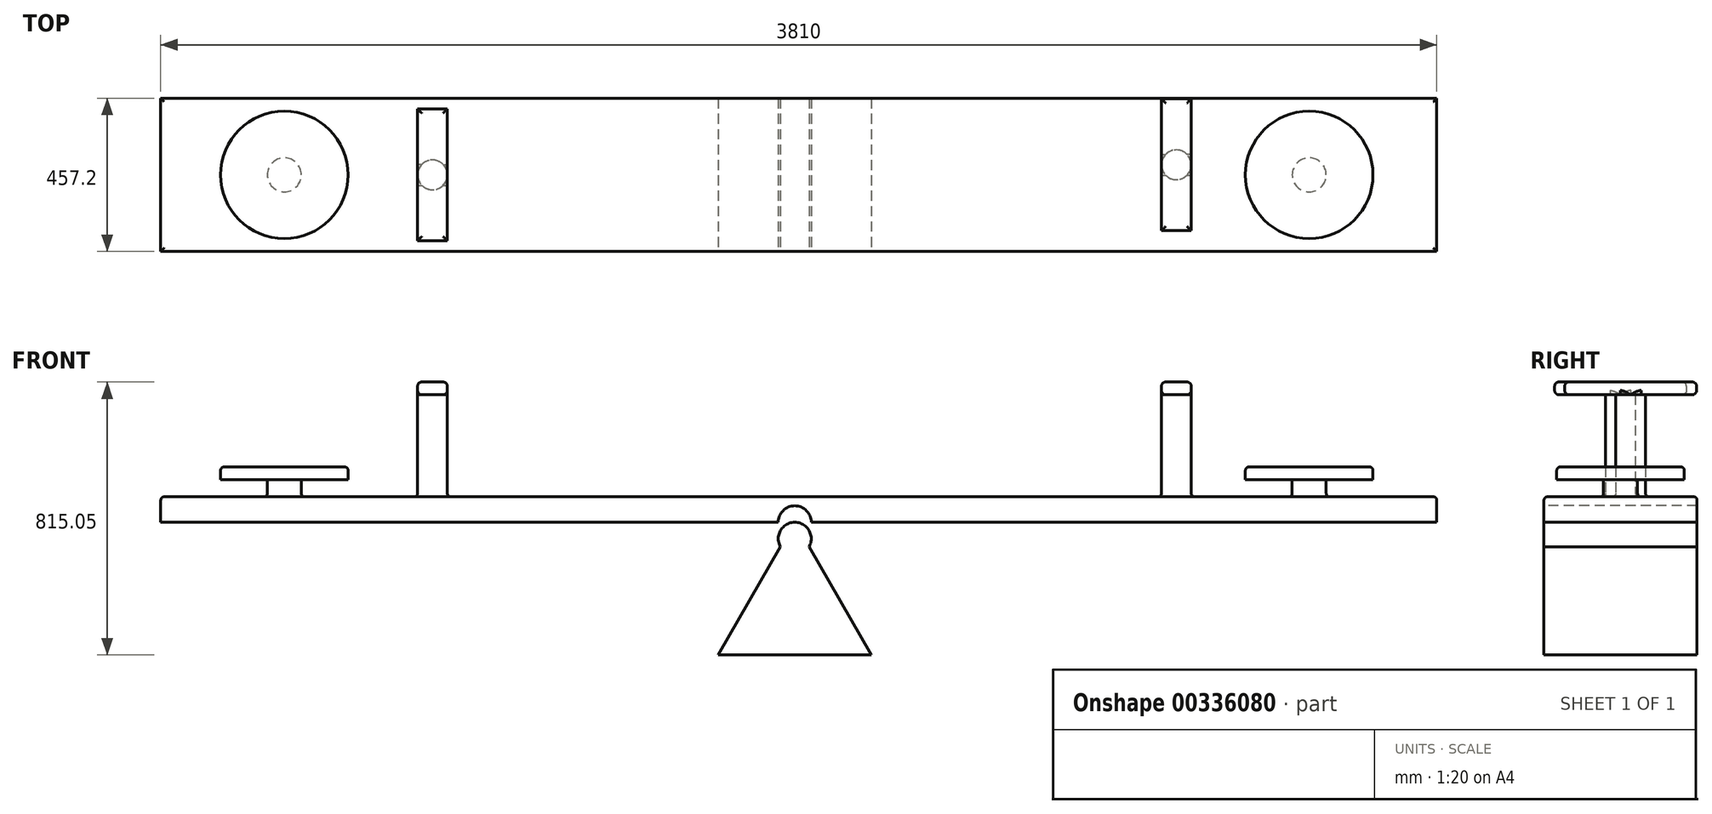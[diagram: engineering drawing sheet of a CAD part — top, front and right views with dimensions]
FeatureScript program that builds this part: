
annotation { "Feature Type Name" : "Feature", "Feature Type Description" : "" }
export const myFeature = defineFeature(function(context is Context, id is Id, definition is map)
    precondition{}
    {
        {
            var Q0;
            Q0=qCreatedBy(makeId("Top.planeOp"),FACE);
            var sketch = newSketch(context, id + "F0", { "sketchPlane" : qUnion([Q0])});
            skLineSegment(sketch, "E0.bottom", {"start": v(228.6, 228.6) * mm, "end": v(-228.6, 228.6) * mm});
            skLineSegment(sketch, "E0.top", {"start": v(228.6, -228.6) * mm, "end": v(-228.6, -228.6) * mm});
            skLineSegment(sketch, "E0.left", {"start": v(228.6, 228.6) * mm, "end": v(228.6, -228.6) * mm});
            skLineSegment(sketch, "E0.right", {"start": v(-228.6, 228.6) * mm, "end": v(-228.6, -228.6) * mm});
            skPoint(sketch, "E0.middle", {"position": v(0, 0) * mm});
            skSolve(sketch);
        }
        {
            var Q0;
            Q0=qCreatedBy(makeId("Front.planeOp"),FACE);
            cPlane(context, id + "F1", {"entities" : qUnion([Q0]), "cplaneType" : CPlaneType.OFFSET, "offset" : 228.6 * mm, "width" : 152.4 * mm, "height" : 152.4 * mm});
        }
        {
            var Q0;
            Q0=qCreatedBy(id+"F1.planeOp",FACE);
            var sketch = newSketch(context, id + "F2", { "sketchPlane" : qUnion([Q0])});
            skLineSegment(sketch, "E1", {"start": v(-228.6, 0) * mm, "end": v(-42.62, 322.13) * mm});
            skLineSegment(sketch, "E2", {"start": v(42.62, 322.13) * mm, "end": v(228.6, 0) * mm});
            skArc(sketch, "E3", {"start": v(42.62, 322.13) * mm, "mid": v(0, 395.95) * mm, "end": v(-42.62, 322.13) * mm});
            skPoint(sketch, "E4.orphan", {"position": v(0, 395.95) * mm});
            skLineSegment(sketch, "E5", {"start": v(-228.6, 0) * mm, "end": v(228.6, 0) * mm});
            skSolve(sketch);
        }
        {
            var Q0;
            Q0=makeQuery(id+"F0.imprint","IMPRINT",FACE,{"disambiguationData":[TD([[makeQuery(id+"F0.imprint","IMPRINT",EDGE,{"derivedFrom":sQuery(id+"F0.wireOp",EDGE,"E0.bottom")}),1.0]])]});
            cPlane(context, id + "F3", {"entities" : qUnion([Q0]), "cplaneType" : CPlaneType.OFFSET, "offset" : 395.95 * mm, "width" : 152.4 * mm, "height" : 152.4 * mm});
        }
        {
            var Q0;
            Q0=qCreatedBy(id+"F3.planeOp",FACE);
            var sketch = newSketch(context, id + "F4", { "sketchPlane" : qUnion([Q0])});
            skLineSegment(sketch, "E6.bottom", {"start": v(1917, 228.6) * mm, "end": v(-1893, 228.6) * mm});
            skLineSegment(sketch, "E6.top", {"start": v(1917, -228.6) * mm, "end": v(-1893, -228.6) * mm});
            skLineSegment(sketch, "E6.left", {"start": v(1917, 228.6) * mm, "end": v(1917, -228.6) * mm});
            skLineSegment(sketch, "E6.right", {"start": v(-1893, 228.6) * mm, "end": v(-1893, -228.6) * mm});
            skPoint(sketch, "E6.middle", {"position": v(12, 0) * mm});
            skSolve(sketch);
        }
        {
            var Q0;
            Q0 = qSketchRegion(id + "F4", true);
            extrude(context, id + "F5", {"entities" : qUnion([Q0]), "depth" : 76.2 * mm});
        }
        {
            var Q0;
            Q0=makeQuery(id+"F5.opExtrude","CAP_FACE",FACE,{"disambiguationData":[OSD([sQuery(id+"F4.wireOp",EDGE,"E6.bottom"),sQuery(id+"F4.wireOp",EDGE,"E6.top"),sQuery(id+"F4.wireOp",EDGE,"E6.left"),sQuery(id+"F4.wireOp",EDGE,"E6.right")])],"isStart":false});
            var sketch = newSketch(context, id + "F6", { "sketchPlane" : qUnion([Q0])});
            skCircle(sketch, "E7", {"center": v(-1524, 0) * mm, "radius": 50.8 * mm});
            skSolve(sketch);
        }
        {
            var Q0;
            Q0 = qSketchRegion(id + "F6", true);
            extrude(context, id + "F7", {"entities" : qUnion([Q0]), "operationType" : NewBodyOperationType.ADD, "depth" : 50.8 * mm});
        }
        {
            var Q0;
            Q0=makeQuery(id+"F7.opExtrude","CAP_FACE",FACE,{"disambiguationData":[OSD([sQuery(id+"F6.wireOp",EDGE,"E7")])],"isStart":false});
            var sketch = newSketch(context, id + "F8", { "sketchPlane" : qUnion([Q0])});
            skCircle(sketch, "E8", {"center": v(-1524, 0) * mm, "radius": 190.5 * mm});
            skSolve(sketch);
        }
        {
            var Q0;
            Q0 = qSketchRegion(id + "F8", true);
            extrude(context, id + "F9", {"entities" : qUnion([Q0]), "operationType" : NewBodyOperationType.ADD, "depth" : 38.1 * mm});
        }
        {
            var Q0;
            Q0=makeQuery(id+"F5.opExtrude","CAP_FACE",FACE,{"disambiguationData":[OSD([sQuery(id+"F4.wireOp",EDGE,"E6.bottom"),sQuery(id+"F4.wireOp",EDGE,"E6.top"),sQuery(id+"F4.wireOp",EDGE,"E6.left"),sQuery(id+"F4.wireOp",EDGE,"E6.right")])],"isStart":false});
            var sketch = newSketch(context, id + "F10", { "sketchPlane" : qUnion([Q0])});
            skCircle(sketch, "E9", {"center": v(1536, 0) * mm, "radius": 50.8 * mm});
            skSolve(sketch);
        }
        {
            var Q0;
            Q0 = qSketchRegion(id + "F10", true);
            extrude(context, id + "F11", {"entities" : qUnion([Q0]), "operationType" : NewBodyOperationType.ADD, "depth" : 50.8 * mm});
        }
        {
            var Q0;
            Q0=makeQuery(id+"F11.opExtrude","CAP_FACE",FACE,{"disambiguationData":[OSD([sQuery(id+"F10.wireOp",EDGE,"E9")])],"isStart":false});
            var sketch = newSketch(context, id + "F12", { "sketchPlane" : qUnion([Q0])});
            skCircle(sketch, "E10", {"center": v(1536, 0) * mm, "radius": 190.5 * mm});
            skSolve(sketch);
        }
        {
            var Q0;
            Q0 = qSketchRegion(id + "F12", true);
            extrude(context, id + "F13", {"entities" : qUnion([Q0]), "operationType" : NewBodyOperationType.ADD, "depth" : 38.1 * mm});
        }
        {
            var Q0;
            Q0 = qSketchRegion(id + "F2", true);
            extrude(context, id + "F14", {"entities" : qUnion([Q0]), "oppositeDirection" : true, "depth" : 457.2 * mm});
        }
        {
            var Q0;
            Q0=makeQuery(id+"F5.opExtrude","SWEPT_FACE",FACE,{"disambiguationData":[OSD([sQuery(id+"F4.wireOp",EDGE,"E6.top")])]});
            var sketch = newSketch(context, id + "F15", { "sketchPlane" : qUnion([Q0])});
            skCircle(sketch, "E11", {"center": v(0, 395.95) * mm, "radius": 49.21 * mm});
            skSolve(sketch);
        }
        {
            var Q0;
            {var subQ0=sQuery(id+"F15.wireOp",EDGE,"E11");var subQ1=makeQuery(id+"F5.opExtrude","CAP_EDGE",EDGE,{"disambiguationData":[OSD([sQuery(id+"F4.wireOp",EDGE,"E6.top")])],"isStart":true});var subQ2=makeQuery(id+"F15.imprint","INTERSECT",VERTEX,{"disambiguationData":[OD(0.0)],"derivedFrom":[subQ1,subQ0]});Q0=makeQuery(id+"F15.imprint","IMPRINT",FACE,{"disambiguationData":[TD([[makeQuery(id+"F15.imprint","IMPRINT",EDGE,{"disambiguationData":[TD([[subQ2,-1.0]])],"derivedFrom":subQ0}),1.0]])]});}
            extrude(context, id + "F16", {"entities" : qUnion([Q0]), "operationType" : NewBodyOperationType.REMOVE, "endBound" : BoundingType.THROUGH_ALL, "oppositeDirection" : true, "depth" : 25.4 * mm});
        }
        {
            var Q0;
            Q0=makeQuery(id+"F5.opExtrude","CAP_FACE",FACE,{"disambiguationData":[OSD([sQuery(id+"F4.wireOp",EDGE,"E6.bottom"),sQuery(id+"F4.wireOp",EDGE,"E6.top"),sQuery(id+"F4.wireOp",EDGE,"E6.left"),sQuery(id+"F4.wireOp",EDGE,"E6.right")])],"isStart":false});
            var sketch = newSketch(context, id + "F17", { "sketchPlane" : qUnion([Q0])});
            skCircle(sketch, "E12", {"center": v(-1081.72, 0) * mm, "radius": 44.45 * mm});
            skSolve(sketch);
        }
        {
            var Q0;
            Q0 = qSketchRegion(id + "F17", true);
            extrude(context, id + "F18", {"entities" : qUnion([Q0]), "operationType" : NewBodyOperationType.ADD, "depth" : 304.8 * mm});
        }
        {
            var Q0;
            Q0=makeQuery(id+"F18.opExtrude","CAP_FACE",FACE,{"disambiguationData":[OSD([sQuery(id+"F17.wireOp",EDGE,"E12")])],"isStart":false});
            var sketch = newSketch(context, id + "F19", { "sketchPlane" : qUnion([Q0])});
            skLineSegment(sketch, "E13.bottom", {"start": v(-1126.17, -196.85) * mm, "end": v(-1037.27, -196.85) * mm});
            skLineSegment(sketch, "E13.top", {"start": v(-1126.17, 196.85) * mm, "end": v(-1037.27, 196.85) * mm});
            skLineSegment(sketch, "E13.left", {"start": v(-1126.17, -196.85) * mm, "end": v(-1126.17, 196.85) * mm});
            skLineSegment(sketch, "E13.right", {"start": v(-1037.27, -196.85) * mm, "end": v(-1037.27, 196.85) * mm});
            skPoint(sketch, "E13.middle", {"position": v(-1081.72, 0) * mm});
            skSolve(sketch);
        }
        {
            var Q0;
            Q0 = qSketchRegion(id + "F19", true);
            extrude(context, id + "F20", {"entities" : qUnion([Q0]), "operationType" : NewBodyOperationType.ADD, "depth" : 38.1 * mm});
        }
        {
            var Q0;
            Q0=makeQuery(id+"F20.opExtrude","CAP_EDGE",EDGE,{"disambiguationData":[OSD([sQuery(id+"F19.wireOp",EDGE,"E13.left")])],"isStart":false});
            var Q1;
            Q1=makeQuery(id+"F20.opExtrude","CAP_EDGE",EDGE,{"disambiguationData":[OSD([sQuery(id+"F19.wireOp",EDGE,"E13.top")])],"isStart":false});
            var Q2;
            Q2=makeQuery(id+"F20.opExtrude","CAP_EDGE",EDGE,{"disambiguationData":[OSD([sQuery(id+"F19.wireOp",EDGE,"E13.right")])],"isStart":false});
            var Q3;
            Q3=makeQuery(id+"F20.opExtrude","CAP_EDGE",EDGE,{"disambiguationData":[OSD([sQuery(id+"F19.wireOp",EDGE,"E13.bottom")])],"isStart":false});
            var Q4;
            {var subQ0=sQuery(id+"F19.wireOp",EDGE,"E13.left");var subQ1=sQuery(id+"F19.wireOp",EDGE,"E13.top");Q4=makeQuery(id+"F20.boolean.opBoolean","SPLIT",EDGE,{"disambiguationData":[TD([makeQuery(id+"F20.opExtrude","SWEPT_FACE",FACE,{"disambiguationData":[OSD([subQ1])]})])],"derivedFrom":makeQuery(id+"F20.opExtrude","CAP_EDGE",EDGE,{"disambiguationData":[OSD([subQ0])],"isStart":true})});}
            var Q5;
            {var subQ0=sQuery(id+"F19.wireOp",EDGE,"E13.bottom");var subQ1=sQuery(id+"F19.wireOp",EDGE,"E13.left");Q5=makeQuery(id+"F20.boolean.opBoolean","SPLIT",EDGE,{"disambiguationData":[TD([makeQuery(id+"F20.opExtrude","SWEPT_FACE",FACE,{"disambiguationData":[OSD([subQ0])]})])],"derivedFrom":makeQuery(id+"F20.opExtrude","CAP_EDGE",EDGE,{"disambiguationData":[OSD([subQ1])],"isStart":true})});}
            var Q6;
            Q6=makeQuery(id+"F20.opExtrude","CAP_EDGE",EDGE,{"disambiguationData":[OSD([sQuery(id+"F19.wireOp",EDGE,"E13.bottom")])],"isStart":true});
            var Q7;
            Q7=makeQuery(id+"F20.opExtrude","CAP_EDGE",EDGE,{"disambiguationData":[OSD([sQuery(id+"F19.wireOp",EDGE,"E13.top")])],"isStart":true});
            var Q8;
            {var subQ0=sQuery(id+"F19.wireOp",EDGE,"E13.right");var subQ1=sQuery(id+"F19.wireOp",EDGE,"E13.top");Q8=makeQuery(id+"F20.boolean.opBoolean","SPLIT",EDGE,{"disambiguationData":[TD([makeQuery(id+"F20.opExtrude","SWEPT_FACE",FACE,{"disambiguationData":[OSD([subQ1])]})])],"derivedFrom":makeQuery(id+"F20.opExtrude","CAP_EDGE",EDGE,{"disambiguationData":[OSD([subQ0])],"isStart":true})});}
            var Q9;
            {var subQ0=sQuery(id+"F19.wireOp",EDGE,"E13.bottom");var subQ1=sQuery(id+"F19.wireOp",EDGE,"E13.right");Q9=makeQuery(id+"F20.boolean.opBoolean","SPLIT",EDGE,{"disambiguationData":[TD([makeQuery(id+"F20.opExtrude","SWEPT_FACE",FACE,{"disambiguationData":[OSD([subQ0])]})])],"derivedFrom":makeQuery(id+"F20.opExtrude","CAP_EDGE",EDGE,{"disambiguationData":[OSD([subQ1])],"isStart":true})});}
            fillet(context, id + "F21", {"entities" : qUnion([Q0, Q1, Q2, Q3, Q4, Q5, Q6, Q7, Q8, Q9]), "radius" : 12.7 * mm, "tangentPropagation" : true, "allowEdgeOverflow" : false});
        }
        {
            var Q0;
            Q0=makeQuery(id+"F5.opExtrude","CAP_FACE",FACE,{"disambiguationData":[OSD([sQuery(id+"F4.wireOp",EDGE,"E6.bottom"),sQuery(id+"F4.wireOp",EDGE,"E6.top"),sQuery(id+"F4.wireOp",EDGE,"E6.left"),sQuery(id+"F4.wireOp",EDGE,"E6.right")])],"isStart":false});
            var sketch = newSketch(context, id + "F22", { "sketchPlane" : qUnion([Q0])});
            skCircle(sketch, "E14", {"center": v(1139.31, 30.13) * mm, "radius": 44.45 * mm});
            skSolve(sketch);
        }
        {
            var Q0;
            Q0 = qSketchRegion(id + "F22", true);
            extrude(context, id + "F23", {"entities" : qUnion([Q0]), "operationType" : NewBodyOperationType.ADD, "depth" : 304.8 * mm});
        }
        {
            var Q0;
            Q0=makeQuery(id+"F23.opExtrude","CAP_FACE",FACE,{"disambiguationData":[OSD([sQuery(id+"F22.wireOp",EDGE,"E14")])],"isStart":false});
            var sketch = newSketch(context, id + "F24", { "sketchPlane" : qUnion([Q0])});
            skLineSegment(sketch, "E15.bottom", {"start": v(1094.86, -166.72) * mm, "end": v(1183.76, -166.72) * mm});
            skLineSegment(sketch, "E15.top", {"start": v(1094.86, 226.98) * mm, "end": v(1183.76, 226.98) * mm});
            skLineSegment(sketch, "E15.left", {"start": v(1094.86, -166.72) * mm, "end": v(1094.86, 226.98) * mm});
            skLineSegment(sketch, "E15.right", {"start": v(1183.76, -166.72) * mm, "end": v(1183.76, 226.98) * mm});
            skPoint(sketch, "E15.middle", {"position": v(1139.31, 30.13) * mm});
            skSolve(sketch);
        }
        {
            var Q0;
            Q0 = qSketchRegion(id + "F24", true);
            extrude(context, id + "F25", {"entities" : qUnion([Q0]), "operationType" : NewBodyOperationType.ADD, "depth" : 38.1 * mm});
        }
        {
            var Q0;
            Q0=makeQuery(id+"F25.opExtrude","CAP_FACE",FACE,{"disambiguationData":[OSD([sQuery(id+"F24.wireOp",EDGE,"E15.bottom"),sQuery(id+"F24.wireOp",EDGE,"E15.top"),sQuery(id+"F24.wireOp",EDGE,"E15.left"),sQuery(id+"F24.wireOp",EDGE,"E15.right")])],"isStart":false});
            var Q1;
            Q1=makeQuery(id+"F25.opExtrude","CAP_EDGE",EDGE,{"disambiguationData":[OSD([sQuery(id+"F24.wireOp",EDGE,"E15.top")])],"isStart":true});
            var Q2;
            {var subQ0=sQuery(id+"F24.wireOp",EDGE,"E15.right");var subQ1=sQuery(id+"F24.wireOp",EDGE,"E15.top");Q2=makeQuery(id+"F25.boolean.opBoolean","SPLIT",EDGE,{"disambiguationData":[TD([makeQuery(id+"F25.opExtrude","SWEPT_FACE",FACE,{"disambiguationData":[OSD([subQ1])]})])],"derivedFrom":makeQuery(id+"F25.opExtrude","CAP_EDGE",EDGE,{"disambiguationData":[OSD([subQ0])],"isStart":true})});}
            var Q3;
            {var subQ0=sQuery(id+"F24.wireOp",EDGE,"E15.right");var subQ1=sQuery(id+"F24.wireOp",EDGE,"E15.bottom");Q3=makeQuery(id+"F25.boolean.opBoolean","SPLIT",EDGE,{"disambiguationData":[TD([makeQuery(id+"F25.opExtrude","SWEPT_FACE",FACE,{"disambiguationData":[OSD([subQ1])]})])],"derivedFrom":makeQuery(id+"F25.opExtrude","CAP_EDGE",EDGE,{"disambiguationData":[OSD([subQ0])],"isStart":true})});}
            var Q4;
            {var subQ0=sQuery(id+"F24.wireOp",EDGE,"E15.left");var subQ1=sQuery(id+"F24.wireOp",EDGE,"E15.top");Q4=makeQuery(id+"F25.boolean.opBoolean","SPLIT",EDGE,{"disambiguationData":[TD([makeQuery(id+"F25.opExtrude","SWEPT_FACE",FACE,{"disambiguationData":[OSD([subQ1])]})])],"derivedFrom":makeQuery(id+"F25.opExtrude","CAP_EDGE",EDGE,{"disambiguationData":[OSD([subQ0])],"isStart":true})});}
            var Q5;
            {var subQ0=sQuery(id+"F24.wireOp",EDGE,"E15.left");var subQ1=sQuery(id+"F24.wireOp",EDGE,"E15.bottom");Q5=makeQuery(id+"F25.boolean.opBoolean","SPLIT",EDGE,{"disambiguationData":[TD([makeQuery(id+"F25.opExtrude","SWEPT_FACE",FACE,{"disambiguationData":[OSD([subQ1])]})])],"derivedFrom":makeQuery(id+"F25.opExtrude","CAP_EDGE",EDGE,{"disambiguationData":[OSD([subQ0])],"isStart":true})});}
            var Q6;
            Q6=makeQuery(id+"F25.opExtrude","CAP_EDGE",EDGE,{"disambiguationData":[OSD([sQuery(id+"F24.wireOp",EDGE,"E15.bottom")])],"isStart":true});
            fillet(context, id + "F26", {"entities" : qUnion([Q0, Q1, Q2, Q3, Q4, Q5, Q6]), "radius" : 12.7 * mm, "tangentPropagation" : true, "allowEdgeOverflow" : false});
        }
        {
            var Q0;
            Q0=makeQuery(id+"F13.opExtrude","CAP_EDGE",EDGE,{"disambiguationData":[OSD([sQuery(id+"F12.wireOp",EDGE,"E10")])],"isStart":false});
            fillet(context, id + "F27", {"entities" : qUnion([Q0]), "radius" : 10.16 * mm, "tangentPropagation" : true, "allowEdgeOverflow" : false});
        }
        {
            var Q0;
            Q0=makeQuery(id+"F9.opExtrude","CAP_EDGE",EDGE,{"disambiguationData":[OSD([sQuery(id+"F8.wireOp",EDGE,"E8")])],"isStart":false});
            var Q1;
            Q1=makeQuery(id+"F5.opExtrude","CAP_FACE",FACE,{"disambiguationData":[OSD([sQuery(id+"F4.wireOp",EDGE,"E6.bottom"),sQuery(id+"F4.wireOp",EDGE,"E6.top"),sQuery(id+"F4.wireOp",EDGE,"E6.left"),sQuery(id+"F4.wireOp",EDGE,"E6.right")])],"isStart":false});
            fillet(context, id + "F28", {"entities" : qUnion([Q0, Q1]), "radius" : 10.16 * mm, "tangentPropagation" : true, "allowEdgeOverflow" : false});
        }
    });
